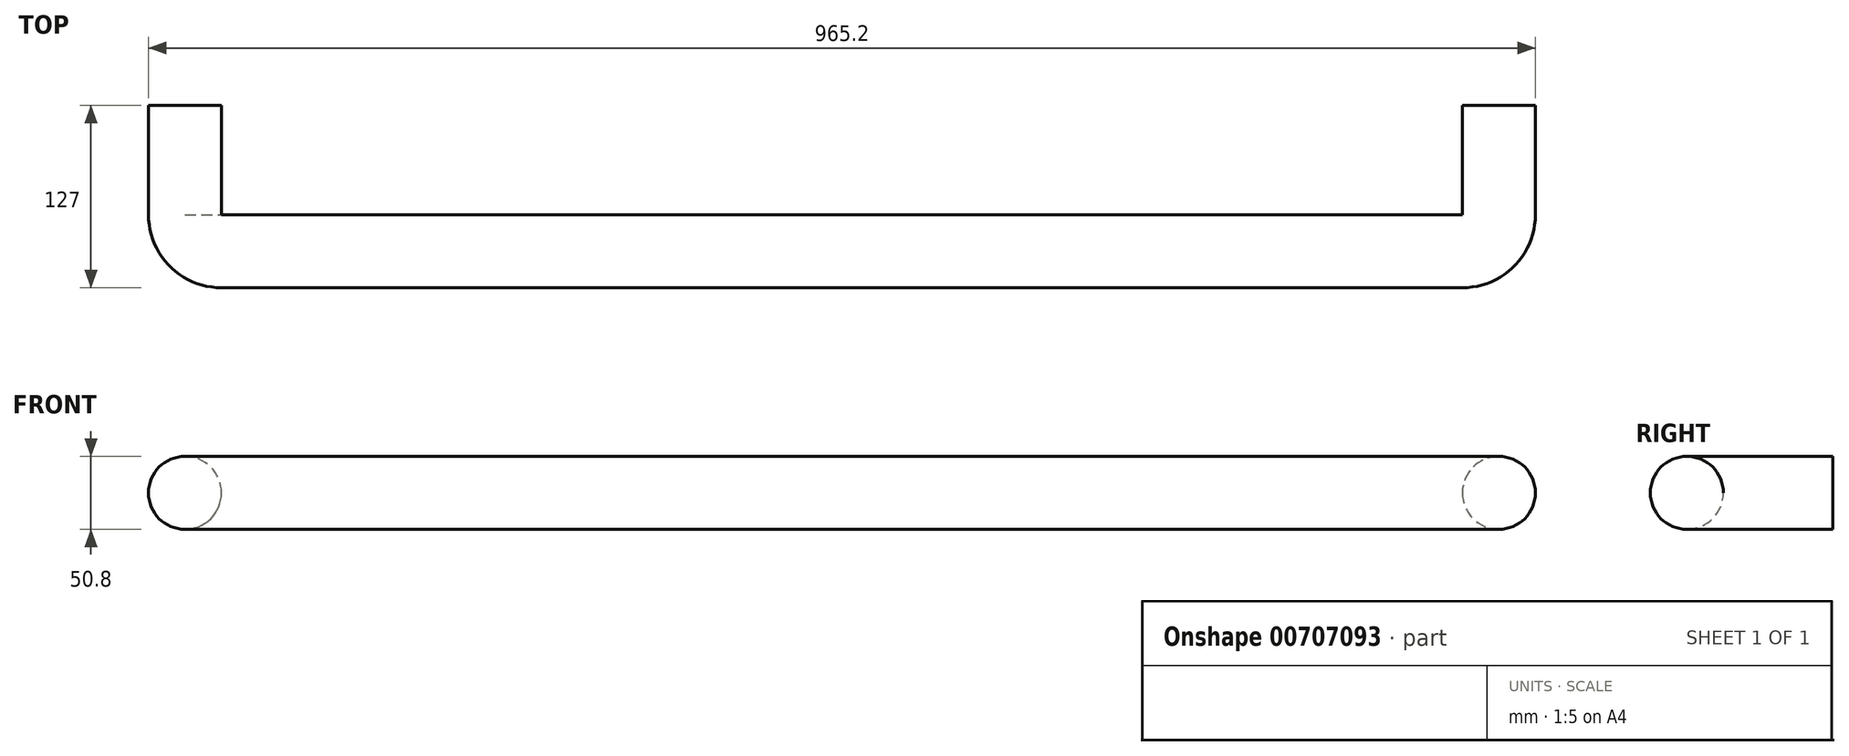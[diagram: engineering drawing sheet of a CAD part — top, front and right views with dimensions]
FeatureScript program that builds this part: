
annotation { "Feature Type Name" : "Feature", "Feature Type Description" : "" }
export const myFeature = defineFeature(function(context is Context, id is Id, definition is map)
    precondition{}
    {
        {
            var Q0;
            Q0=qCreatedBy(makeId("Top.planeOp"),FACE);
            var sketch = newSketch(context, id + "F0", { "sketchPlane" : qUnion([Q0])});
            skLineSegment(sketch, "E0", {"start": v(0, 0) * mm, "end": v(0, -76.2) * mm});
            skLineSegment(sketch, "E1", {"start": v(25.4, -101.6) * mm, "end": v(889, -101.6) * mm});
            skLineSegment(sketch, "E2", {"start": v(914.4, -76.2) * mm, "end": v(914.4, 0) * mm});
            skPoint(sketch, "E3.visualSharp", {"position": v(0, -101.6) * mm});
            skArc(sketch, "E3.filletArc", {"start": v(0, -76.2) * mm, "mid": v(7.44, -94.16) * mm, "end": v(25.4, -101.6) * mm});
            skPoint(sketch, "E4.visualSharp", {"position": v(914.4, -101.6) * mm});
            skArc(sketch, "E4.filletArc", {"start": v(889, -101.6) * mm, "mid": v(906.96, -94.16) * mm, "end": v(914.4, -76.2) * mm});
            skSolve(sketch);
        }
        {
            var Q0;
            Q0=qCreatedBy(makeId("Front.planeOp"),FACE);
            var sketch = newSketch(context, id + "F1", { "sketchPlane" : qUnion([Q0])});
            skCircle(sketch, "E5", {"center": v(0, 0) * mm, "radius": 25.4 * mm});
            skSolve(sketch);
        }
        {
            var Q0;
            Q0=makeQuery(id+"F1.imprint","IMPRINT",FACE,{"disambiguationData":[TD([[makeQuery(id+"F1.imprint","IMPRINT",EDGE,{"derivedFrom":sQuery(id+"F1.wireOp",EDGE,"E5")}),1.0]])]});
            var Q1;
            Q1=sQuery(id+"F0.wireOp",EDGE,"E1");
            var Q2;
            Q2=sQuery(id+"F0.wireOp",EDGE,"E0");
            var Q3;
            Q3=sQuery(id+"F0.wireOp",EDGE,"E3.filletArc");
            var Q4;
            Q4=sQuery(id+"F0.wireOp",EDGE,"E4.filletArc");
            var Q5;
            Q5=sQuery(id+"F0.wireOp",EDGE,"E2");
            sweep(context, id + "F2", {"profiles" : qUnion([Q0]), "path" : qUnion([Q1, Q2, Q3, Q4, Q5])});
        }
    });
